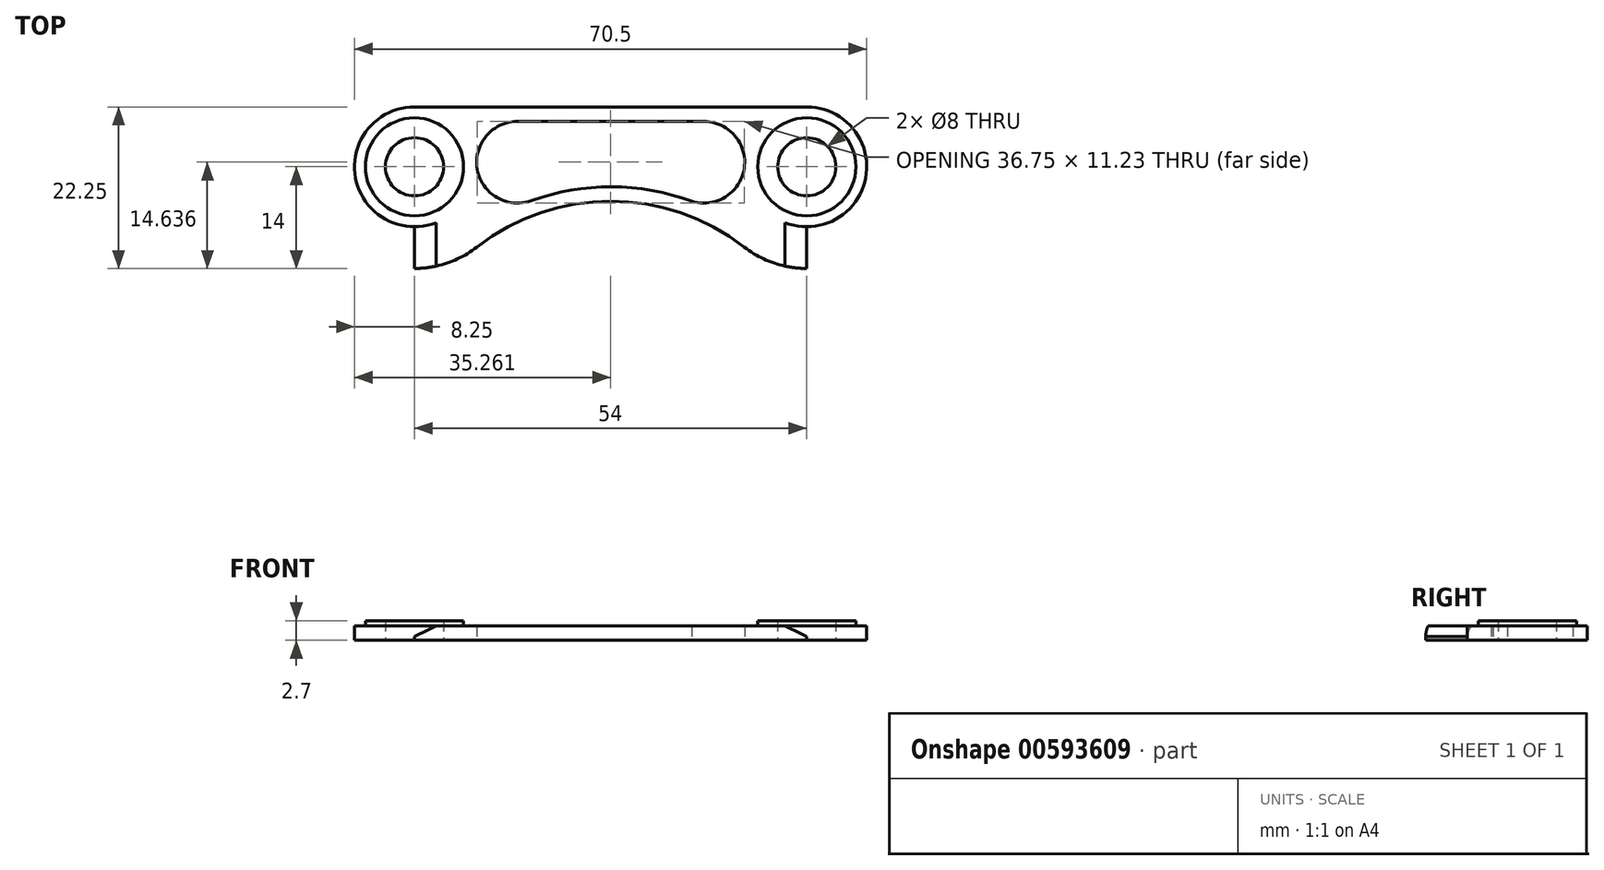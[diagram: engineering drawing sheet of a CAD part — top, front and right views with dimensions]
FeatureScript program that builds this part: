
annotation { "Feature Type Name" : "Feature", "Feature Type Description" : "" }
export const myFeature = defineFeature(function(context is Context, id is Id, definition is map)
    precondition{}
    {
        {
            var Q0;
            Q0=qCreatedBy(makeId("Top.planeOp"),FACE);
            var sketch = newSketch(context, id + "F0", { "sketchPlane" : qUnion([Q0])});
            skCircle(sketch, "E0", {"center": v(0, 0) * mm, "radius": 4 * mm});
            skLineSegment(sketch, "E1", {"start": v(0, 0) * mm, "end": v(54, 0) * mm, "construction": true});
            skCircle(sketch, "E2", {"center": v(54, 0) * mm, "radius": 4 * mm});
            skArc(sketch, "E3", {"start": v(0, 8.25) * mm, "mid": v(-8.25, 0) * mm, "end": v(0, -8.25) * mm});
            skArc(sketch, "E4", {"start": v(54, -8.25) * mm, "mid": v(62.25, 0) * mm, "end": v(54, 8.25) * mm});
            skLineSegment(sketch, "E5", {"start": v(0, 8.25) * mm, "end": v(54, 8.25) * mm});
            skArc(sketch, "E6.0", {"start": v(45.42, -11.06) * mm, "mid": v(49.46, -13.24) * mm, "end": v(54, -14) * mm});
            skArc(sketch, "E7.0", {"start": v(0, -14) * mm, "mid": v(4.54, -13.24) * mm, "end": v(8.58, -11.06) * mm});
            skLineSegment(sketch, "E8", {"start": v(54, 0) * mm, "end": v(54, -14) * mm});
            skLineSegment(sketch, "E9", {"start": v(0, 0) * mm, "end": v(0, -14) * mm});
            skArc(sketch, "E10", {"start": v(45.42, -11.06) * mm, "mid": v(27, -4.75) * mm, "end": v(8.58, -11.06) * mm});
            skLineSegment(sketch, "E11.0", {"start": v(27, -4.75) * mm, "end": v(40.83, -4.75) * mm});
            skLineSegment(sketch, "E12.0", {"start": v(0, 6.25) * mm, "end": v(54, 6.25) * mm});
            skArc(sketch, "E13.0", {"start": v(46.64, -9.48) * mm, "mid": v(27, -2.75) * mm, "end": v(7.36, -9.48) * mm});
            skCircle(sketch, "E14", {"center": v(14.18, 0.63) * mm, "radius": 5.62 * mm});
            skCircle(sketch, "E15", {"center": v(39.82, 0.63) * mm, "radius": 5.62 * mm});
            skSolve(sketch);
        }
        {
            var Q0;
            Q0=makeQuery(id+"F0.imprint","IMPRINT",FACE,{"disambiguationData":[TD([[makeQuery(id+"F0.imprint","IMPRINT",EDGE,{"derivedFrom":sQuery(id+"F0.wireOp",EDGE,"E0")}),-1.0]])]});
            var Q1;
            Q1=makeQuery(id+"F0.imprint","IMPRINT",FACE,{"disambiguationData":[TD([[makeQuery(id+"F0.imprint","IMPRINT",EDGE,{"derivedFrom":sQuery(id+"F0.wireOp",EDGE,"E2")}),-1.0]])]});
            extrude(context, id + "F1", {"entities" : qUnion([Q0, Q1]), "depth" : 2 * mm, "offsetDistance" : 25 * mm});
        }
        {
            var Q0;
            Q0=makeQuery(id+"F1.opExtrude","CAP_FACE",FACE,{"disambiguationData":[OSD([sQuery(id+"F0.wireOp",EDGE,"E0"),sQuery(id+"F0.wireOp",EDGE,"E2"),sQuery(id+"F0.wireOp",EDGE,"E3"),sQuery(id+"F0.wireOp",EDGE,"E4"),sQuery(id+"F0.wireOp",EDGE,"E5"),sQuery(id+"F0.wireOp",EDGE,"E6.0"),sQuery(id+"F0.wireOp",EDGE,"E7.0"),sQuery(id+"F0.wireOp",EDGE,"E8"),sQuery(id+"F0.wireOp",EDGE,"E9"),sQuery(id+"F0.wireOp",EDGE,"E10")])],"isStart":false});
            var sketch = newSketch(context, id + "F2", { "sketchPlane" : qUnion([Q0])});
            skCircle(sketch, "E16", {"center": v(0, 0) * mm, "radius": 6.75 * mm});
            skCircle(sketch, "E17", {"center": v(54, 0) * mm, "radius": 6.75 * mm});
            skCircle(sketch, "E18", {"center": v(0, 0) * mm, "radius": 4 * mm});
            skCircle(sketch, "E19", {"center": v(54, 0) * mm, "radius": 4 * mm});
            skSolve(sketch);
        }
        {
            var Q0;
            Q0=makeQuery(id+"F2.imprint","IMPRINT",FACE,{"disambiguationData":[TD([[makeQuery(id+"F2.imprint","IMPRINT",EDGE,{"derivedFrom":sQuery(id+"F2.wireOp",EDGE,"E16")}),1.0]])]});
            var Q1;
            Q1=makeQuery(id+"F2.imprint","IMPRINT",FACE,{"disambiguationData":[TD([[makeQuery(id+"F2.imprint","IMPRINT",EDGE,{"derivedFrom":sQuery(id+"F2.wireOp",EDGE,"E17")}),1.0]])]});
            extrude(context, id + "F3", {"entities" : qUnion([Q0, Q1]), "operationType" : NewBodyOperationType.ADD, "depth" : .7 * mm, "offsetDistance" : 25 * mm});
        }
        {
            var Q0;
            Q0=makeQuery(id+"F1.opExtrude","CAP_EDGE",EDGE,{"disambiguationData":[OSD([sQuery(id+"F0.wireOp",EDGE,"E9")])],"isStart":false});
            var Q1;
            Q1=makeQuery(id+"F1.opExtrude","CAP_EDGE",EDGE,{"disambiguationData":[OSD([sQuery(id+"F0.wireOp",EDGE,"E8")])],"isStart":false});
            chamfer(context, id + "F4", {"entities" : qUnion([Q0, Q1]), "chamferType" : ChamferType.TWO_OFFSETS, "width1" : 3 * mm, "oppositeDirection" : false, "width2" : 1.5 * mm, "tangentPropagation" : true});
        }
    });
